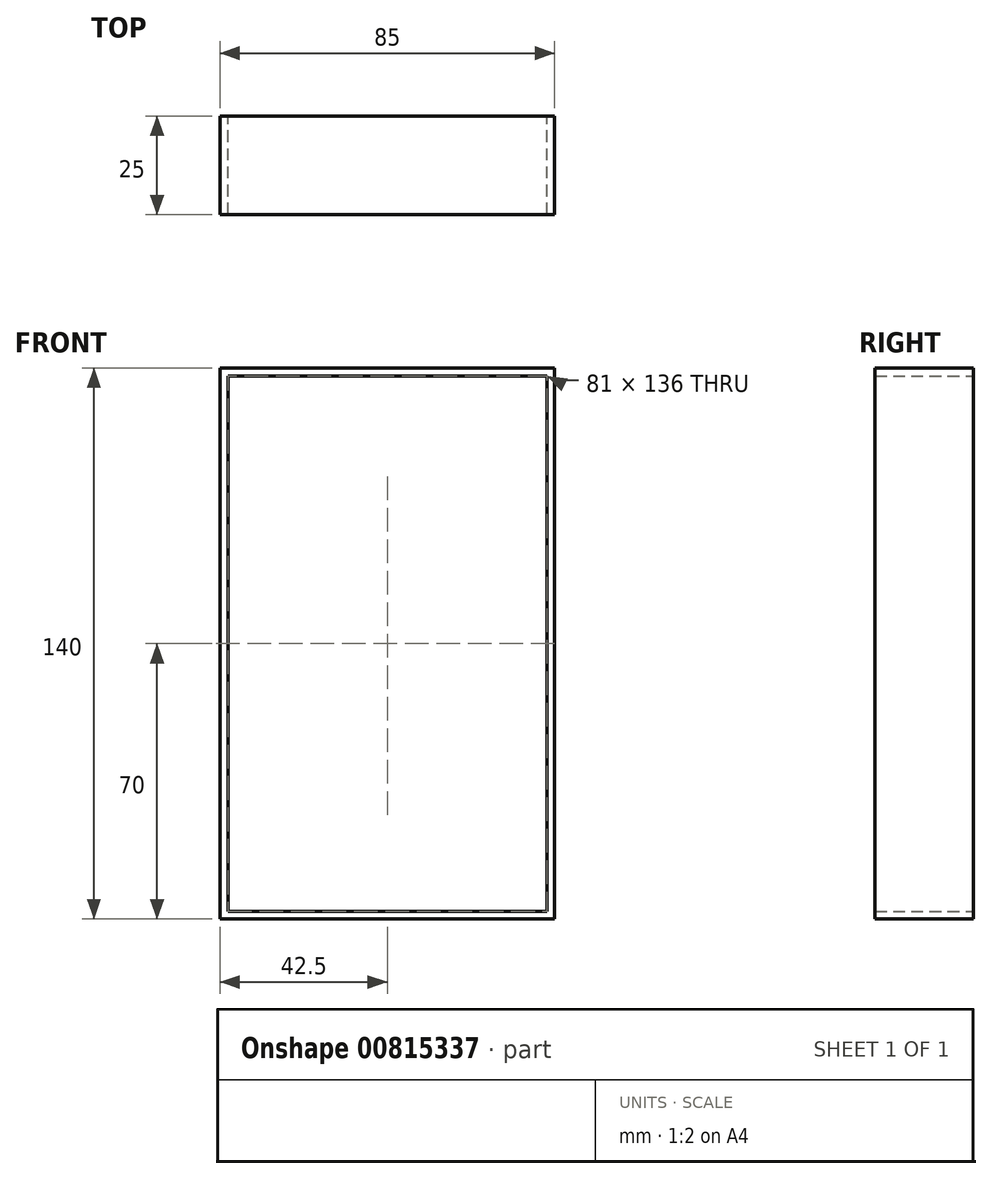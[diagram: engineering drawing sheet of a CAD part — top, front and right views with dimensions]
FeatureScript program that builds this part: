
annotation { "Feature Type Name" : "Feature", "Feature Type Description" : "" }
export const myFeature = defineFeature(function(context is Context, id is Id, definition is map)
    precondition{}
    {
        {
            var Q0;
            Q0=qCreatedBy(makeId("Front.planeOp"),FACE);
            var sketch = newSketch(context, id + "F0", { "sketchPlane" : qUnion([Q0])});
            skLineSegment(sketch, "E0.bottom", {"start": v(42.5, -70) * mm, "end": v(-42.5, -70) * mm});
            skLineSegment(sketch, "E0.top", {"start": v(42.5, 70) * mm, "end": v(-42.5, 70) * mm});
            skLineSegment(sketch, "E0.left", {"start": v(42.5, -70) * mm, "end": v(42.5, 70) * mm});
            skLineSegment(sketch, "E0.right", {"start": v(-42.5, -70) * mm, "end": v(-42.5, 70) * mm});
            skPoint(sketch, "E0.middle", {"position": v(0, 0) * mm});
            skLineSegment(sketch, "E1.bottom", {"start": v(40.5, -68) * mm, "end": v(-40.5, -68) * mm});
            skLineSegment(sketch, "E1.top", {"start": v(40.5, 68) * mm, "end": v(-40.5, 68) * mm});
            skLineSegment(sketch, "E1.left", {"start": v(40.5, -68) * mm, "end": v(40.5, 68) * mm});
            skLineSegment(sketch, "E1.right", {"start": v(-40.5, -68) * mm, "end": v(-40.5, 68) * mm});
            skSolve(sketch);
        }
        {
            var Q0;
            Q0 = qSketchRegion(id + "F0", true);
            extrude(context, id + "F1", {"entities" : qUnion([Q0]), "depth" : 25 * mm, "offsetDistance" : 25 * mm});
        }
    });
